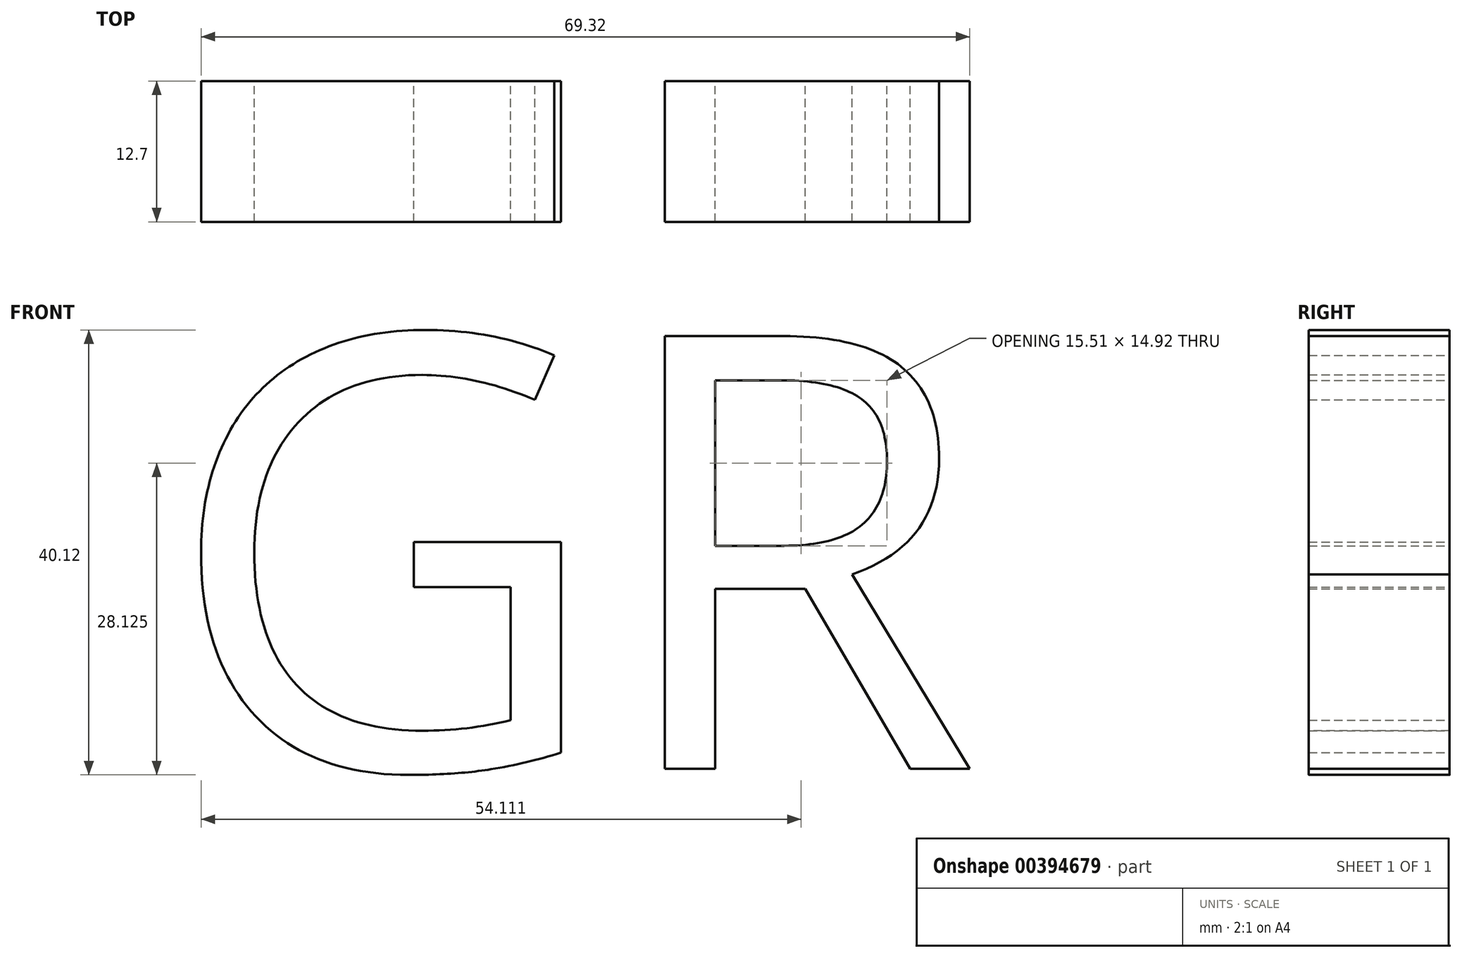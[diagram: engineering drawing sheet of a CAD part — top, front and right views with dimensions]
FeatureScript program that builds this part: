
annotation { "Feature Type Name" : "Feature", "Feature Type Description" : "" }
export const myFeature = defineFeature(function(context is Context, id is Id, definition is map)
    precondition{}
    {
        {
            var Q0;
            Q0=qCreatedBy(makeId("Front.planeOp"),FACE);
            var sketch = newSketch(context, id + "F0", { "sketchPlane" : qUnion([Q0])});
            skText(sketch, "E0", { "text": "GR", "fontName": "OpenSans-Regular.ttf"});
            const initialGuessF0  = {"E0": [-0.03216, -0.0217, 1, 0, 0.03936]};
            skSetInitialGuess(sketch, initialGuessF0);
            skSolve(sketch);
        }
        {
            var Q0;
            Q0 = qSketchRegion(id + "F0", true);
            extrude(context, id + "F1", {"entities" : qUnion([Q0]), "depth" : 12.7 * mm});
        }
    });
